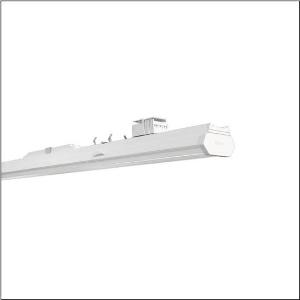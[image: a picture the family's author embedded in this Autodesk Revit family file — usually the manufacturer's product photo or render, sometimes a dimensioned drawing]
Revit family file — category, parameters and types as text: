
# Revit family: licross_21_protected_mo_52td11dn48xg
name_source: partatom
category: Lighting Fixtures
units: mm (PartAtom-declared; Revit-internal decimal feet)

## family parameters
Cut with Voids When Loaded = No
Host = Face
Light Source = No
Part Type = Normal
Room Calculation Point = No
Round Connector Dimension = Use Diameter
Shared = No

## types (1)
- --- (1 x LED, 8000 lm, 45.5 W, 4000K)
    Apparent Load = 46 VA
    CIE Flux Codes = 83 94 98 100 100
    Color Rendering = 80
    Color Temperature = 4000K
    Default Elevation = 1800 mm
    Description = Licross 21 Protected MO, luminaire insert, of sheet steel, galvanised, coil coated, white, length: 1.500mm, width: 90mm, height: 103mm, LED rated luminous flux: 8.000lm, light colour: 840, SDCM (Standard Deviation of Colour Matching)MacAdam ≤ 3 SDCM (initial), control gear: DALI 2, with plug, 5-pole, with phase selection, mains connection: 220..240V, AC, 50/60Hz, rated input power: 46W, internal wiring halogen-free, primary light control with lens, of plastic, primary optical cover: cover, of PMMA, light emission: direct distribution, primary light characteristic: symmetric, protection rating (complete): IP54, insulation class (complete): insulation class I (protective earthing), certification: CE, ENEC, VDE, UKCA, protection symbol: D if used in an environment with non-conductive dust loads with corresponding accessories, impact resistance: IK06, permissible ambient temperature for indoor applications: -25..+45°C, corresponds to IFS (International Featured Standards) requirements for safety and quality in the food industry, reducing of maximum allowable ambient temperature of 5°C with ceiling mounting, LABS conformity tested according to VDMA 24364:2018-05, The light source and the operating device comply with the requirements of the Ecodesign Regulation (EU) 2019/2020 and are replaceable in accordance with this regulation, packaging unit: 1 piece
    Height = 92 mm
    Lamp = 1 x LED
    Lamp Light Flux = 8000 lm
    Lamp Power = 45.5 W
    Lamp count = 1
    Length = 1500 mm
    Luminous efficacy = 176 lm/W
    Manufacturer = Siteco
    ModVariant = No
    Model = 52TD11DN48XG
    Mounting Place = Ceiling
    Mounting Type = Pendant
    Number of Poles = 1
    OnlyDefault = Yes
    Power Factor = 1
    Product Name = Licross 21 Protected MO
    Product group = luminaire insert | ceiling pendant
    ProductGroupID = 901
    Protection Class = Protection class I
    Protection Degree = IP 54
    RLX_Detail_Level = 1
    RLX_Emergency_Light_Flux = 0 lm
    RLX_Emergency_Type = 0
    RLX_Emergency_Type_DB = No
    RlxData = <blob elided: 24337 chars, md5=beead847>
    Socket = socket
    Standby Power = 0 W
    System Light Flux = 8000 lm
    System Power = 46 W
    Type Comments = factory setting: luminous flux: 100 % | dim-lin: 254 | 307 mA
    Type Image = l_1256148.jpg
    URL = http://relux.com
    VarID = @adj_129981
    Voltage = 0 V
    Weight = 0.00 kg
    Width = 88 mm

## geometry (parser evidence)
native form markers: Blend x4, Sweep x10
no freeform markers — native parametric forms only
